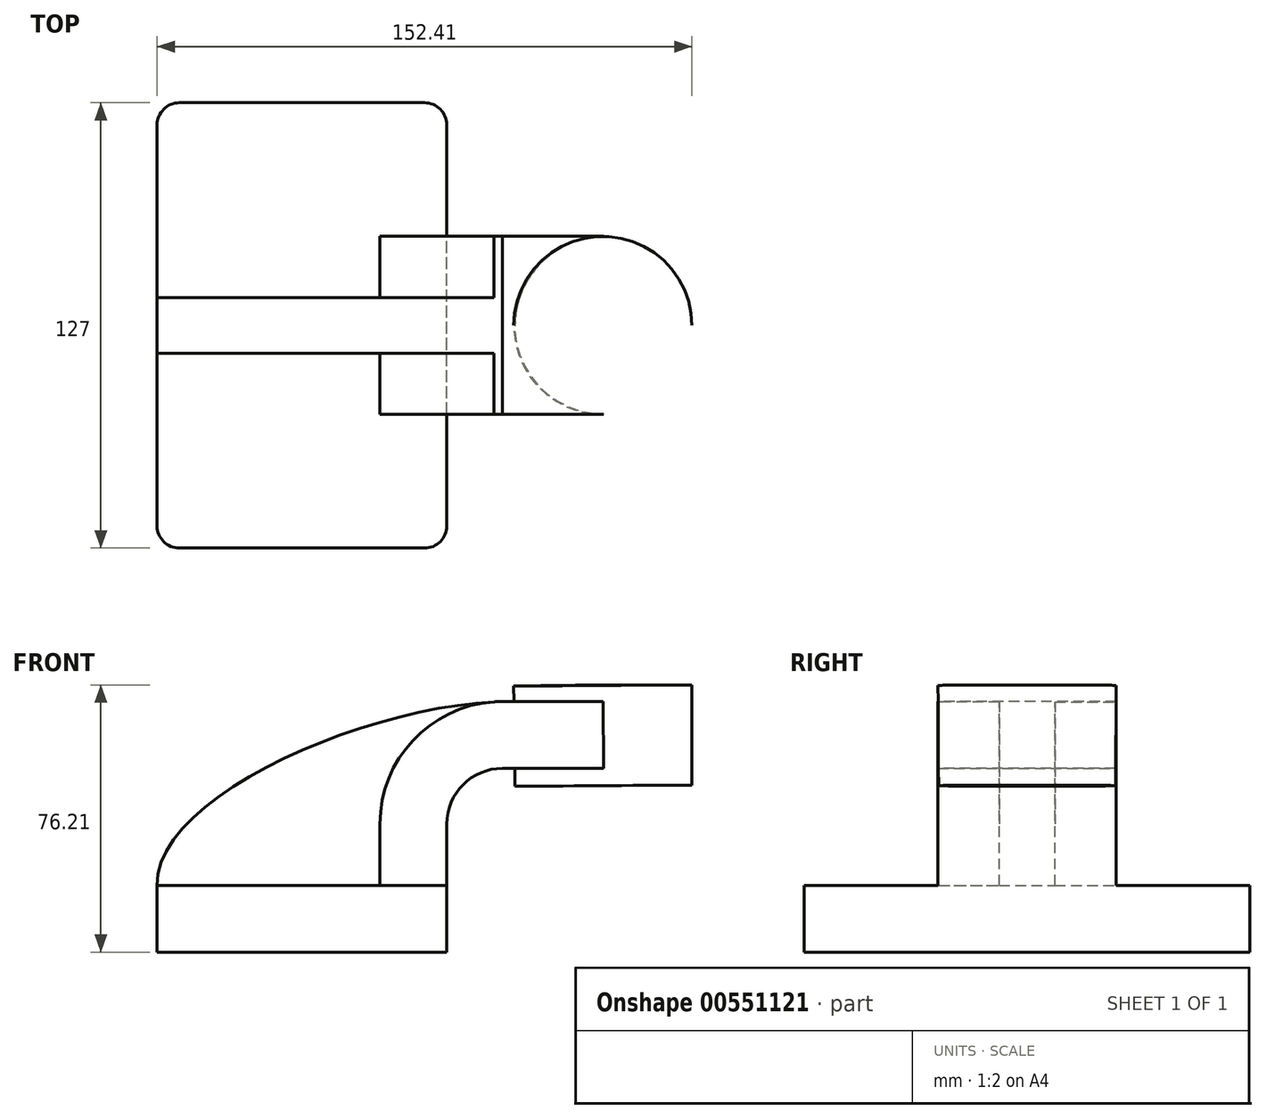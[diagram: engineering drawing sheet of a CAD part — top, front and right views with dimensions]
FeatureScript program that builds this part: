
annotation { "Feature Type Name" : "Feature", "Feature Type Description" : "" }
export const myFeature = defineFeature(function(context is Context, id is Id, definition is map)
    precondition{}
    {
        {
            var Q0;
            Q0=qCreatedBy(makeId("Front.planeOp"),FACE);
            var sketch = newSketch(context, id + "F0", { "sketchPlane" : qUnion([Q0])});
            skLineSegment(sketch, "E0.bottom", {"start": v(41.27, 9.53) * mm, "end": v(-41.28, 9.53) * mm});
            skLineSegment(sketch, "E0.top", {"start": v(41.28, -9.52) * mm, "end": v(-41.27, -9.52) * mm});
            skLineSegment(sketch, "E0.left", {"start": v(41.28, 9.53) * mm, "end": v(41.28, -9.52) * mm});
            skLineSegment(sketch, "E0.right", {"start": v(-41.28, 9.53) * mm, "end": v(-41.27, -9.52) * mm});
            skPoint(sketch, "E0.middle", {"position": v(0, 0) * mm});
            skLineSegment(sketch, "E1.bottom", {"start": v(111.12, 66.68) * mm, "end": v(60.32, 66.68) * mm});
            skLineSegment(sketch, "E1.top", {"start": v(111.12, 38.1) * mm, "end": v(60.32, 38.1) * mm});
            skLineSegment(sketch, "E1.left", {"start": v(111.12, 66.68) * mm, "end": v(111.12, 38.1) * mm});
            skLineSegment(sketch, "E1.right", {"start": v(60.32, 66.68) * mm, "end": v(60.32, 38.1) * mm});
            skPoint(sketch, "E1.middle", {"position": v(85.72, 52.39) * mm});
            skLineSegment(sketch, "E2", {"start": v(41.27, 9.53) * mm, "end": v(41.27, 27) * mm});
            skArc(sketch, "E3", {"start": v(41.27, 27) * mm, "mid": v(45.92, 38.23) * mm, "end": v(57.15, 42.88) * mm});
            skLineSegment(sketch, "E4", {"start": v(57.15, 42.88) * mm, "end": v(85.92, 42.88) * mm});
            skLineSegment(sketch, "E5.0", {"start": v(57.15, 61.93) * mm, "end": v(85.92, 61.93) * mm});
            skArc(sketch, "E5.1", {"start": v(22.23, 27) * mm, "mid": v(32.45, 51.7) * mm, "end": v(57.15, 61.93) * mm});
            skLineSegment(sketch, "E5.2", {"start": v(22.22, 9.53) * mm, "end": v(22.22, 27) * mm});
            skFitSpline(sketch, "E6", {"points": [v(-41.28, 9.52) * mm, v(57.15, 61.93) * mm], "startDerivative": vector(-1.86, 76.85) * mm, "endDerivative": vector(113.33, 2.47) * mm});
            skLineSegment(sketch, "E7", {"start": v(85.72, 66.68) * mm, "end": v(85.92, 38.1) * mm});
            skSolve(sketch);
        }
        {
            var Q0;
            Q0=makeQuery(id+"F0.imprint","IMPRINT",FACE,{"disambiguationData":[TD([[makeQuery(id+"F0.imprint","IMPRINT",EDGE,{"derivedFrom":sQuery(id+"F0.wireOp",EDGE,"E0.top")}),-1.0]])]});
            extrude(context, id + "F1", {"entities" : qUnion([Q0]), "endBound" : BoundingType.SYMMETRIC, "depth" : 127 * mm, "offsetDistance" : 25.4 * mm});
        }
        {
            var Q0;
            {var subQ1=sQuery(id+"F0.wireOp",EDGE,"E2");Q0=makeQuery(id+"F0.imprint","IMPRINT",FACE,{"disambiguationData":[TD([[makeQuery(id+"F0.imprint","IMPRINT",EDGE,{"derivedFrom":subQ1}),1.0]])]});}
            var Q1;
            {var subQ0=sQuery(id+"F0.wireOp",EDGE,"E5.0");var subQ1=sQuery(id+"F0.wireOp",EDGE,"E1.right");var subQ2=makeQuery(id+"F0.imprint","INTERSECT",VERTEX,{"derivedFrom":[subQ1,subQ0]});Q1=makeQuery(id+"F0.imprint","IMPRINT",FACE,{"disambiguationData":[TD([[makeQuery(id+"F0.imprint","IMPRINT",EDGE,{"disambiguationData":[TD([[subQ2,-1.0]])],"derivedFrom":subQ1}),1.0]])]});}
            extrude(context, id + "F2", {"entities" : qUnion([Q0, Q1]), "operationType" : NewBodyOperationType.ADD, "endBound" : BoundingType.SYMMETRIC, "depth" : 50.8 * mm, "offsetDistance" : 25.4 * mm});
        }
        {
            var Q0;
            {var subQ3=sQuery(id+"F0.wireOp",EDGE,"E5.2");Q0=makeQuery(id+"F0.imprint","IMPRINT",FACE,{"disambiguationData":[TD([[makeQuery(id+"F0.imprint","IMPRINT",EDGE,{"derivedFrom":subQ3}),1.0]])]});}
            extrude(context, id + "F3", {"entities" : qUnion([Q0]), "operationType" : NewBodyOperationType.ADD, "endBound" : BoundingType.SYMMETRIC, "depth" : 15.88 * mm, "offsetDistance" : 25.4 * mm});
        }
        {
            var Q0;
            {var subQ4=sQuery(id+"F0.wireOp",EDGE,"E1.left");Q0=makeQuery(id+"F0.imprint","IMPRINT",FACE,{"disambiguationData":[TD([[makeQuery(id+"F0.imprint","IMPRINT",EDGE,{"derivedFrom":subQ4}),-1.0]])]});}
            var Q1;
            Q1=sQuery(id+"F0.wireOp",EDGE,"E7");
            revolve(context, id + "F4", {"operationType" : NewBodyOperationType.ADD, "entities" : qUnion([Q0]), "axis" : qUnion([Q1]), "revolveType" : RevolveType.FULL});
        }
        {
            var Q0;
            Q0=makeQuery(id+"F1.opExtrude","CAP_EDGE",EDGE,{"disambiguationData":[OSD([sQuery(id+"F0.wireOp",EDGE,"E0.left")])],"isStart":false});
            var Q1;
            Q1=makeQuery(id+"F1.opExtrude","CAP_EDGE",EDGE,{"disambiguationData":[OSD([sQuery(id+"F0.wireOp",EDGE,"E0.right")])],"isStart":false});
            var Q2;
            Q2=makeQuery(id+"F1.opExtrude","CAP_EDGE",EDGE,{"disambiguationData":[OSD([sQuery(id+"F0.wireOp",EDGE,"E0.right")])],"isStart":true});
            var Q3;
            Q3=makeQuery(id+"F1.opExtrude","CAP_EDGE",EDGE,{"disambiguationData":[OSD([sQuery(id+"F0.wireOp",EDGE,"E0.left")])],"isStart":true});
            fillet(context, id + "F5", {"entities" : qUnion([Q0, Q1, Q2, Q3]), "radius" : 6.35 * mm, "tangentPropagation" : true, "allowEdgeOverflow" : false});
        }
    });
